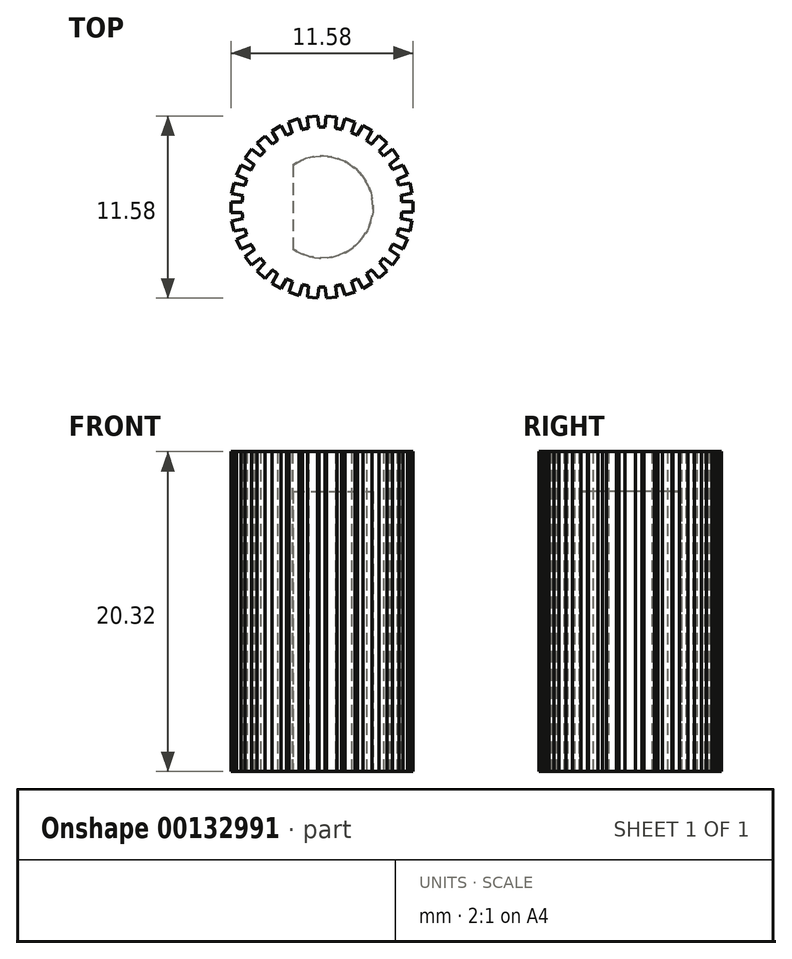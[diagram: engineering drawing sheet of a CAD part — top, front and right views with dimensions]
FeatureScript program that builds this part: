
annotation { "Feature Type Name" : "Feature", "Feature Type Description" : "" }
export const myFeature = defineFeature(function(context is Context, id is Id, definition is map)
    precondition{}
    {
        {
            var Q0;
            Q0=qCreatedBy(makeId("Top.planeOp"),FACE);
            var sketch = newSketch(context, id + "F0", { "sketchPlane" : qUnion([Q0])});
            skArc(sketch, "E0", {"start": v(-1.84, -2.66) * mm, "mid": v(3.24, 0) * mm, "end": v(-1.84, 2.66) * mm});
            skLineSegment(sketch, "E1", {"start": v(-1.84, -0.03) * mm, "end": v(-1.84, 2.66) * mm});
            skLineSegment(sketch, "E2", {"start": v(-1.84, -0.03) * mm, "end": v(-1.84, -2.66) * mm});
            skPoint(sketch, "E3.start.orphan", {"position": v(3.24, 0) * mm});
            skArc(sketch, "E4", {"start": v(-5.07, -0.34) * mm, "mid": v(-5.05, -0.54) * mm, "end": v(-5.03, -0.73) * mm});
            skLineSegment(sketch, "E5", {"start": v(-5.07, 0.33) * mm, "end": v(-5.79, 0.33) * mm});
            skLineSegment(sketch, "E6", {"start": v(-5.79, 0.33) * mm, "end": v(-5.79, 0) * mm});
            skLineSegment(sketch, "E7", {"start": v(-5.79, 0) * mm, "end": v(-5.79, -0.34) * mm});
            skLineSegment(sketch, "E8", {"start": v(-5.79, -0.34) * mm, "end": v(-5.07, -0.34) * mm});
            skLineSegment(sketch, "E9.1.0", {"start": v(-5.03, -0.73) * mm, "end": v(-5.73, -0.88) * mm});
            skLineSegment(sketch, "E9.1.1", {"start": v(-5.66, -1.2) * mm, "end": v(-5.59, -1.53) * mm});
            skLineSegment(sketch, "E9.1.2", {"start": v(-5.73, -0.88) * mm, "end": v(-5.66, -1.2) * mm});
            skLineSegment(sketch, "E9.1.3", {"start": v(-5.59, -1.53) * mm, "end": v(-4.89, -1.38) * mm});
            skLineSegment(sketch, "E9.2.0", {"start": v(-4.77, -1.76) * mm, "end": v(-5.42, -2.05) * mm});
            skLineSegment(sketch, "E9.2.1", {"start": v(-5.29, -2.35) * mm, "end": v(-5.15, -2.66) * mm});
            skLineSegment(sketch, "E9.2.2", {"start": v(-5.42, -2.05) * mm, "end": v(-5.29, -2.35) * mm});
            skLineSegment(sketch, "E9.2.3", {"start": v(-5.15, -2.66) * mm, "end": v(-4.5, -2.37) * mm});
            skLineSegment(sketch, "E9.3.0", {"start": v(-4.3, -2.71) * mm, "end": v(-4.87, -3.13) * mm});
            skLineSegment(sketch, "E9.3.1", {"start": v(-4.68, -3.4) * mm, "end": v(-4.48, -3.67) * mm});
            skLineSegment(sketch, "E9.3.2", {"start": v(-4.87, -3.13) * mm, "end": v(-4.68, -3.4) * mm});
            skLineSegment(sketch, "E9.3.3", {"start": v(-4.48, -3.67) * mm, "end": v(-3.9, -3.25) * mm});
            skLineSegment(sketch, "E9.4.0", {"start": v(-3.64, -3.55) * mm, "end": v(-4.12, -4.08) * mm});
            skLineSegment(sketch, "E9.4.1", {"start": v(-3.87, -4.3) * mm, "end": v(-3.62, -4.53) * mm});
            skLineSegment(sketch, "E9.4.2", {"start": v(-4.12, -4.08) * mm, "end": v(-3.87, -4.3) * mm});
            skLineSegment(sketch, "E9.4.3", {"start": v(-3.62, -4.53) * mm, "end": v(-3.14, -4) * mm});
            skLineSegment(sketch, "E9.5.0", {"start": v(-2.82, -4.23) * mm, "end": v(-3.18, -4.85) * mm});
            skLineSegment(sketch, "E9.5.1", {"start": v(-2.9, -5.01) * mm, "end": v(-2.6, -5.18) * mm});
            skLineSegment(sketch, "E9.5.2", {"start": v(-3.18, -4.85) * mm, "end": v(-2.9, -5.01) * mm});
            skLineSegment(sketch, "E9.5.3", {"start": v(-2.6, -5.18) * mm, "end": v(-2.24, -4.56) * mm});
            skLineSegment(sketch, "E9.6.0", {"start": v(-1.88, -4.72) * mm, "end": v(-2.1, -5.4) * mm});
            skLineSegment(sketch, "E9.6.1", {"start": v(-1.79, -5.5) * mm, "end": v(-1.47, -5.6) * mm});
            skLineSegment(sketch, "E9.6.2", {"start": v(-2.1, -5.4) * mm, "end": v(-1.79, -5.5) * mm});
            skLineSegment(sketch, "E9.6.3", {"start": v(-1.47, -5.6) * mm, "end": v(-1.24, -4.93) * mm});
            skLineSegment(sketch, "E9.7.0", {"start": v(-0.86, -5) * mm, "end": v(-0.93, -5.72) * mm});
            skLineSegment(sketch, "E9.7.1", {"start": v(-0.6, -5.75) * mm, "end": v(-0.27, -5.79) * mm});
            skLineSegment(sketch, "E9.7.2", {"start": v(-0.93, -5.72) * mm, "end": v(-0.6, -5.75) * mm});
            skLineSegment(sketch, "E9.7.3", {"start": v(-0.27, -5.79) * mm, "end": v(-0.2, -5.08) * mm});
            skLineSegment(sketch, "E9.8.0", {"start": v(0.2, -5.08) * mm, "end": v(0.28, -5.79) * mm});
            skLineSegment(sketch, "E9.8.1", {"start": v(0.6, -5.75) * mm, "end": v(0.94, -5.72) * mm});
            skLineSegment(sketch, "E9.8.2", {"start": v(0.28, -5.79) * mm, "end": v(0.6, -5.75) * mm});
            skLineSegment(sketch, "E9.8.3", {"start": v(0.94, -5.72) * mm, "end": v(0.87, -5) * mm});
            skLineSegment(sketch, "E9.9.0", {"start": v(1.25, -4.92) * mm, "end": v(1.47, -5.6) * mm});
            skLineSegment(sketch, "E9.9.1", {"start": v(1.79, -5.5) * mm, "end": v(2.1, -5.4) * mm});
            skLineSegment(sketch, "E9.9.2", {"start": v(1.47, -5.6) * mm, "end": v(1.79, -5.5) * mm});
            skLineSegment(sketch, "E9.9.3", {"start": v(2.1, -5.4) * mm, "end": v(1.89, -4.72) * mm});
            skLineSegment(sketch, "E9.10.0", {"start": v(2.25, -4.56) * mm, "end": v(2.6, -5.18) * mm});
            skLineSegment(sketch, "E9.10.1", {"start": v(2.9, -5.01) * mm, "end": v(3.19, -4.84) * mm});
            skLineSegment(sketch, "E9.10.2", {"start": v(2.6, -5.18) * mm, "end": v(2.9, -5.01) * mm});
            skLineSegment(sketch, "E9.10.3", {"start": v(3.19, -4.84) * mm, "end": v(2.83, -4.22) * mm});
            skLineSegment(sketch, "E9.11.0", {"start": v(3.15, -3.99) * mm, "end": v(3.63, -4.52) * mm});
            skLineSegment(sketch, "E9.11.1", {"start": v(3.87, -4.3) * mm, "end": v(4.12, -4.07) * mm});
            skLineSegment(sketch, "E9.11.2", {"start": v(3.63, -4.52) * mm, "end": v(3.87, -4.3) * mm});
            skLineSegment(sketch, "E9.11.3", {"start": v(4.12, -4.07) * mm, "end": v(3.64, -3.54) * mm});
            skLineSegment(sketch, "E9.12.0", {"start": v(3.9, -3.25) * mm, "end": v(4.49, -3.67) * mm});
            skLineSegment(sketch, "E9.12.1", {"start": v(4.68, -3.4) * mm, "end": v(4.88, -3.13) * mm});
            skLineSegment(sketch, "E9.12.2", {"start": v(4.49, -3.67) * mm, "end": v(4.68, -3.4) * mm});
            skLineSegment(sketch, "E9.12.3", {"start": v(4.88, -3.13) * mm, "end": v(4.3, -2.7) * mm});
            skLineSegment(sketch, "E9.13.0", {"start": v(4.5, -2.36) * mm, "end": v(5.15, -2.65) * mm});
            skLineSegment(sketch, "E9.13.1", {"start": v(5.29, -2.35) * mm, "end": v(5.42, -2.04) * mm});
            skLineSegment(sketch, "E9.13.2", {"start": v(5.15, -2.65) * mm, "end": v(5.29, -2.35) * mm});
            skLineSegment(sketch, "E9.13.3", {"start": v(5.42, -2.04) * mm, "end": v(4.77, -1.75) * mm});
            skLineSegment(sketch, "E9.14.0", {"start": v(4.89, -1.38) * mm, "end": v(5.6, -1.53) * mm});
            skLineSegment(sketch, "E9.14.1", {"start": v(5.66, -1.2) * mm, "end": v(5.73, -0.87) * mm});
            skLineSegment(sketch, "E9.14.2", {"start": v(5.6, -1.53) * mm, "end": v(5.66, -1.2) * mm});
            skLineSegment(sketch, "E9.14.3", {"start": v(5.73, -0.87) * mm, "end": v(5.03, -0.72) * mm});
            skLineSegment(sketch, "E9.15.0", {"start": v(5.07, -0.33) * mm, "end": v(5.79, -0.33) * mm});
            skLineSegment(sketch, "E9.15.1", {"start": v(5.79, 0) * mm, "end": v(5.79, 0.34) * mm});
            skLineSegment(sketch, "E9.15.2", {"start": v(5.79, -0.33) * mm, "end": v(5.79, 0) * mm});
            skLineSegment(sketch, "E9.15.3", {"start": v(5.79, 0.34) * mm, "end": v(5.07, 0.34) * mm});
            skLineSegment(sketch, "E9.16.0", {"start": v(5.03, 0.73) * mm, "end": v(5.73, 0.88) * mm});
            skLineSegment(sketch, "E9.16.1", {"start": v(5.66, 1.2) * mm, "end": v(5.59, 1.53) * mm});
            skLineSegment(sketch, "E9.16.2", {"start": v(5.73, 0.88) * mm, "end": v(5.66, 1.2) * mm});
            skLineSegment(sketch, "E9.16.3", {"start": v(5.59, 1.53) * mm, "end": v(4.89, 1.38) * mm});
            skLineSegment(sketch, "E9.17.0", {"start": v(4.77, 1.76) * mm, "end": v(5.42, 2.05) * mm});
            skLineSegment(sketch, "E9.17.1", {"start": v(5.29, 2.35) * mm, "end": v(5.15, 2.66) * mm});
            skLineSegment(sketch, "E9.17.2", {"start": v(5.42, 2.05) * mm, "end": v(5.29, 2.35) * mm});
            skLineSegment(sketch, "E9.17.3", {"start": v(5.15, 2.66) * mm, "end": v(4.5, 2.37) * mm});
            skLineSegment(sketch, "E9.18.0", {"start": v(4.3, 2.71) * mm, "end": v(4.87, 3.13) * mm});
            skLineSegment(sketch, "E9.18.1", {"start": v(4.68, 3.4) * mm, "end": v(4.48, 3.67) * mm});
            skLineSegment(sketch, "E9.18.2", {"start": v(4.87, 3.13) * mm, "end": v(4.68, 3.4) * mm});
            skLineSegment(sketch, "E9.18.3", {"start": v(4.48, 3.67) * mm, "end": v(3.9, 3.25) * mm});
            skLineSegment(sketch, "E9.19.0", {"start": v(3.64, 3.55) * mm, "end": v(4.12, 4.08) * mm});
            skLineSegment(sketch, "E9.19.1", {"start": v(3.87, 4.3) * mm, "end": v(3.62, 4.53) * mm});
            skLineSegment(sketch, "E9.19.2", {"start": v(4.12, 4.08) * mm, "end": v(3.87, 4.3) * mm});
            skLineSegment(sketch, "E9.19.3", {"start": v(3.62, 4.53) * mm, "end": v(3.14, 4) * mm});
            skLineSegment(sketch, "E9.20.0", {"start": v(2.82, 4.23) * mm, "end": v(3.18, 4.85) * mm});
            skLineSegment(sketch, "E9.20.1", {"start": v(2.9, 5.01) * mm, "end": v(2.6, 5.18) * mm});
            skLineSegment(sketch, "E9.20.2", {"start": v(3.18, 4.85) * mm, "end": v(2.9, 5.01) * mm});
            skLineSegment(sketch, "E9.20.3", {"start": v(2.6, 5.18) * mm, "end": v(2.24, 4.56) * mm});
            skLineSegment(sketch, "E9.21.0", {"start": v(1.88, 4.72) * mm, "end": v(2.1, 5.4) * mm});
            skLineSegment(sketch, "E9.21.1", {"start": v(1.79, 5.5) * mm, "end": v(1.47, 5.6) * mm});
            skLineSegment(sketch, "E9.21.2", {"start": v(2.1, 5.4) * mm, "end": v(1.79, 5.5) * mm});
            skLineSegment(sketch, "E9.21.3", {"start": v(1.47, 5.6) * mm, "end": v(1.24, 4.93) * mm});
            skLineSegment(sketch, "E9.22.0", {"start": v(0.86, 5) * mm, "end": v(0.93, 5.72) * mm});
            skLineSegment(sketch, "E9.22.1", {"start": v(0.6, 5.75) * mm, "end": v(0.27, 5.79) * mm});
            skLineSegment(sketch, "E9.22.2", {"start": v(0.93, 5.72) * mm, "end": v(0.6, 5.75) * mm});
            skLineSegment(sketch, "E9.22.3", {"start": v(0.27, 5.79) * mm, "end": v(0.2, 5.08) * mm});
            skLineSegment(sketch, "E9.23.0", {"start": v(-0.2, 5.08) * mm, "end": v(-0.28, 5.79) * mm});
            skLineSegment(sketch, "E9.23.1", {"start": v(-0.6, 5.75) * mm, "end": v(-0.94, 5.72) * mm});
            skLineSegment(sketch, "E9.23.2", {"start": v(-0.28, 5.79) * mm, "end": v(-0.6, 5.75) * mm});
            skLineSegment(sketch, "E9.23.3", {"start": v(-0.94, 5.72) * mm, "end": v(-0.87, 5) * mm});
            skLineSegment(sketch, "E9.24.0", {"start": v(-1.25, 4.92) * mm, "end": v(-1.47, 5.6) * mm});
            skLineSegment(sketch, "E9.24.1", {"start": v(-1.79, 5.5) * mm, "end": v(-2.1, 5.4) * mm});
            skLineSegment(sketch, "E9.24.2", {"start": v(-1.47, 5.6) * mm, "end": v(-1.79, 5.5) * mm});
            skLineSegment(sketch, "E9.24.3", {"start": v(-2.1, 5.4) * mm, "end": v(-1.89, 4.72) * mm});
            skLineSegment(sketch, "E9.25.0", {"start": v(-2.25, 4.56) * mm, "end": v(-2.6, 5.18) * mm});
            skLineSegment(sketch, "E9.25.1", {"start": v(-2.9, 5.01) * mm, "end": v(-3.19, 4.84) * mm});
            skLineSegment(sketch, "E9.25.2", {"start": v(-2.6, 5.18) * mm, "end": v(-2.9, 5.01) * mm});
            skLineSegment(sketch, "E9.25.3", {"start": v(-3.19, 4.84) * mm, "end": v(-2.83, 4.22) * mm});
            skLineSegment(sketch, "E9.26.0", {"start": v(-3.15, 3.99) * mm, "end": v(-3.63, 4.52) * mm});
            skLineSegment(sketch, "E9.26.1", {"start": v(-3.87, 4.3) * mm, "end": v(-4.12, 4.07) * mm});
            skLineSegment(sketch, "E9.26.2", {"start": v(-3.63, 4.52) * mm, "end": v(-3.87, 4.3) * mm});
            skLineSegment(sketch, "E9.26.3", {"start": v(-4.12, 4.07) * mm, "end": v(-3.64, 3.54) * mm});
            skLineSegment(sketch, "E9.27.0", {"start": v(-3.9, 3.25) * mm, "end": v(-4.49, 3.67) * mm});
            skLineSegment(sketch, "E9.27.1", {"start": v(-4.68, 3.4) * mm, "end": v(-4.88, 3.13) * mm});
            skLineSegment(sketch, "E9.27.2", {"start": v(-4.49, 3.67) * mm, "end": v(-4.68, 3.4) * mm});
            skLineSegment(sketch, "E9.27.3", {"start": v(-4.88, 3.13) * mm, "end": v(-4.3, 2.7) * mm});
            skLineSegment(sketch, "E9.28.0", {"start": v(-4.5, 2.36) * mm, "end": v(-5.15, 2.65) * mm});
            skLineSegment(sketch, "E9.28.1", {"start": v(-5.29, 2.35) * mm, "end": v(-5.42, 2.04) * mm});
            skLineSegment(sketch, "E9.28.2", {"start": v(-5.15, 2.65) * mm, "end": v(-5.29, 2.35) * mm});
            skLineSegment(sketch, "E9.28.3", {"start": v(-5.42, 2.04) * mm, "end": v(-4.77, 1.75) * mm});
            skLineSegment(sketch, "E9.29.0", {"start": v(-4.89, 1.38) * mm, "end": v(-5.6, 1.53) * mm});
            skLineSegment(sketch, "E9.29.1", {"start": v(-5.66, 1.2) * mm, "end": v(-5.73, 0.87) * mm});
            skLineSegment(sketch, "E9.29.2", {"start": v(-5.6, 1.53) * mm, "end": v(-5.66, 1.2) * mm});
            skLineSegment(sketch, "E9.29.3", {"start": v(-5.73, 0.87) * mm, "end": v(-5.03, 0.72) * mm});
            skArc(sketch, "E10.trimOffspring", {"start": v(-5.03, 0.72) * mm, "mid": v(-5.05, 0.53) * mm, "end": v(-5.07, 0.33) * mm});
            skArc(sketch, "E11.trimOffspring", {"start": v(-4.77, 1.75) * mm, "mid": v(-4.83, 1.57) * mm, "end": v(-4.89, 1.38) * mm});
            skArc(sketch, "E12.trimOffspring", {"start": v(-4.3, 2.7) * mm, "mid": v(-4.4, 2.54) * mm, "end": v(-4.5, 2.36) * mm});
            skArc(sketch, "E13.trimOffspring", {"start": v(-3.64, 3.54) * mm, "mid": v(-3.78, 3.4) * mm, "end": v(-3.9, 3.25) * mm});
            skArc(sketch, "E14.trimOffspring", {"start": v(-2.83, 4.22) * mm, "mid": v(-2.99, 4.1) * mm, "end": v(-3.15, 3.99) * mm});
            skArc(sketch, "E15.trimOffspring", {"start": v(-1.89, 4.72) * mm, "mid": v(-2.07, 4.64) * mm, "end": v(-2.25, 4.56) * mm});
            skArc(sketch, "E16.trimOffspring", {"start": v(-0.87, 5) * mm, "mid": v(-1.06, 4.97) * mm, "end": v(-1.25, 4.92) * mm});
            skArc(sketch, "E17.trimOffspring", {"start": v(0.2, 5.08) * mm, "mid": v(0, 5.08) * mm, "end": v(-0.2, 5.08) * mm});
            skArc(sketch, "E18.trimOffspring", {"start": v(1.24, 4.93) * mm, "mid": v(1.05, 4.97) * mm, "end": v(0.86, 5) * mm});
            skArc(sketch, "E19.trimOffspring", {"start": v(2.24, 4.56) * mm, "mid": v(2.06, 4.64) * mm, "end": v(1.88, 4.72) * mm});
            skArc(sketch, "E20.trimOffspring", {"start": v(3.14, 4) * mm, "mid": v(2.98, 4.11) * mm, "end": v(2.82, 4.23) * mm});
            skArc(sketch, "E21.trimOffspring", {"start": v(3.9, 3.25) * mm, "mid": v(3.77, 3.4) * mm, "end": v(3.64, 3.55) * mm});
            skArc(sketch, "E22.trimOffspring", {"start": v(4.5, 2.37) * mm, "mid": v(4.4, 2.54) * mm, "end": v(4.3, 2.71) * mm});
            skArc(sketch, "E23.trimOffspring", {"start": v(4.89, 1.38) * mm, "mid": v(4.83, 1.57) * mm, "end": v(4.77, 1.76) * mm});
            skArc(sketch, "E24.trimOffspring", {"start": v(5.07, 0.34) * mm, "mid": v(5.05, 0.54) * mm, "end": v(5.03, 0.73) * mm});
            skArc(sketch, "E25.trimOffspring", {"start": v(5.03, -0.72) * mm, "mid": v(5.05, -0.53) * mm, "end": v(5.07, -0.33) * mm});
            skArc(sketch, "E26.trimOffspring", {"start": v(4.77, -1.75) * mm, "mid": v(4.83, -1.57) * mm, "end": v(4.89, -1.38) * mm});
            skArc(sketch, "E27.trimOffspring", {"start": v(4.3, -2.7) * mm, "mid": v(4.4, -2.54) * mm, "end": v(4.5, -2.36) * mm});
            skArc(sketch, "E28.trimOffspring", {"start": v(3.64, -3.54) * mm, "mid": v(3.78, -3.4) * mm, "end": v(3.9, -3.25) * mm});
            skArc(sketch, "E29.trimOffspring", {"start": v(2.83, -4.22) * mm, "mid": v(2.99, -4.1) * mm, "end": v(3.15, -3.99) * mm});
            skArc(sketch, "E30.trimOffspring", {"start": v(1.89, -4.72) * mm, "mid": v(2.07, -4.64) * mm, "end": v(2.25, -4.56) * mm});
            skArc(sketch, "E31.trimOffspring", {"start": v(0.87, -5) * mm, "mid": v(1.06, -4.97) * mm, "end": v(1.25, -4.92) * mm});
            skArc(sketch, "E32.trimOffspring", {"start": v(-0.2, -5.08) * mm, "mid": v(0, -5.08) * mm, "end": v(0.2, -5.08) * mm});
            skArc(sketch, "E33.trimOffspring", {"start": v(-1.24, -4.93) * mm, "mid": v(-1.05, -4.97) * mm, "end": v(-0.86, -5) * mm});
            skArc(sketch, "E34.trimOffspring", {"start": v(-2.24, -4.56) * mm, "mid": v(-2.06, -4.64) * mm, "end": v(-1.88, -4.72) * mm});
            skArc(sketch, "E35.trimOffspring", {"start": v(-3.14, -4) * mm, "mid": v(-2.98, -4.11) * mm, "end": v(-2.82, -4.23) * mm});
            skArc(sketch, "E36.trimOffspring", {"start": v(-3.9, -3.25) * mm, "mid": v(-3.77, -3.4) * mm, "end": v(-3.64, -3.55) * mm});
            skArc(sketch, "E37.trimOffspring", {"start": v(-4.5, -2.37) * mm, "mid": v(-4.4, -2.54) * mm, "end": v(-4.3, -2.71) * mm});
            skArc(sketch, "E38.trimOffspring", {"start": v(-4.89, -1.38) * mm, "mid": v(-4.83, -1.57) * mm, "end": v(-4.77, -1.76) * mm});
            skSolve(sketch);
        }
        {
            var Q0;
            Q0=makeQuery(id+"F0.imprint","IMPRINT",FACE,{"disambiguationData":[TD([[makeQuery(id+"F0.imprint","IMPRINT",EDGE,{"derivedFrom":sQuery(id+"F0.wireOp",EDGE,"E0")}),-1.0]])]});
            extrude(context, id + "F1", {"entities" : qUnion([Q0]), "depth" : 15.24 * mm});
        }
        {
            var Q0;
            Q0=makeQuery(id+"F1.opExtrude","CAP_FACE",FACE,{"disambiguationData":[OSD([sQuery(id+"F0.wireOp",EDGE,"E0"),sQuery(id+"F0.wireOp",EDGE,"E1"),sQuery(id+"F0.wireOp",EDGE,"E2"),sQuery(id+"F0.wireOp",EDGE,"E4"),sQuery(id+"F0.wireOp",EDGE,"E5"),sQuery(id+"F0.wireOp",EDGE,"E6"),sQuery(id+"F0.wireOp",EDGE,"E7"),sQuery(id+"F0.wireOp",EDGE,"E8"),sQuery(id+"F0.wireOp",EDGE,"E9.1.0"),sQuery(id+"F0.wireOp",EDGE,"E9.1.1"),sQuery(id+"F0.wireOp",EDGE,"E9.1.2"),sQuery(id+"F0.wireOp",EDGE,"E9.1.3"),sQuery(id+"F0.wireOp",EDGE,"E9.2.0"),sQuery(id+"F0.wireOp",EDGE,"E9.2.1"),sQuery(id+"F0.wireOp",EDGE,"E9.2.2"),sQuery(id+"F0.wireOp",EDGE,"E9.2.3"),sQuery(id+"F0.wireOp",EDGE,"E9.3.0"),sQuery(id+"F0.wireOp",EDGE,"E9.3.1"),sQuery(id+"F0.wireOp",EDGE,"E9.3.2"),sQuery(id+"F0.wireOp",EDGE,"E9.3.3"),sQuery(id+"F0.wireOp",EDGE,"E9.4.0"),sQuery(id+"F0.wireOp",EDGE,"E9.4.1"),sQuery(id+"F0.wireOp",EDGE,"E9.4.2"),sQuery(id+"F0.wireOp",EDGE,"E9.4.3"),sQuery(id+"F0.wireOp",EDGE,"E9.5.0"),sQuery(id+"F0.wireOp",EDGE,"E9.5.1"),sQuery(id+"F0.wireOp",EDGE,"E9.5.2"),sQuery(id+"F0.wireOp",EDGE,"E9.5.3"),sQuery(id+"F0.wireOp",EDGE,"E9.6.0"),sQuery(id+"F0.wireOp",EDGE,"E9.6.1"),sQuery(id+"F0.wireOp",EDGE,"E9.6.2"),sQuery(id+"F0.wireOp",EDGE,"E9.6.3"),sQuery(id+"F0.wireOp",EDGE,"E9.7.0"),sQuery(id+"F0.wireOp",EDGE,"E9.7.1"),sQuery(id+"F0.wireOp",EDGE,"E9.7.2"),sQuery(id+"F0.wireOp",EDGE,"E9.7.3"),sQuery(id+"F0.wireOp",EDGE,"E9.8.0"),sQuery(id+"F0.wireOp",EDGE,"E9.8.1"),sQuery(id+"F0.wireOp",EDGE,"E9.8.2"),sQuery(id+"F0.wireOp",EDGE,"E9.8.3"),sQuery(id+"F0.wireOp",EDGE,"E9.9.0"),sQuery(id+"F0.wireOp",EDGE,"E9.9.1"),sQuery(id+"F0.wireOp",EDGE,"E9.9.2"),sQuery(id+"F0.wireOp",EDGE,"E9.9.3"),sQuery(id+"F0.wireOp",EDGE,"E9.10.0"),sQuery(id+"F0.wireOp",EDGE,"E9.10.1"),sQuery(id+"F0.wireOp",EDGE,"E9.10.2"),sQuery(id+"F0.wireOp",EDGE,"E9.10.3"),sQuery(id+"F0.wireOp",EDGE,"E9.11.0"),sQuery(id+"F0.wireOp",EDGE,"E9.11.1"),sQuery(id+"F0.wireOp",EDGE,"E9.11.2"),sQuery(id+"F0.wireOp",EDGE,"E9.11.3"),sQuery(id+"F0.wireOp",EDGE,"E9.12.0"),sQuery(id+"F0.wireOp",EDGE,"E9.12.1"),sQuery(id+"F0.wireOp",EDGE,"E9.12.2"),sQuery(id+"F0.wireOp",EDGE,"E9.12.3"),sQuery(id+"F0.wireOp",EDGE,"E9.13.0"),sQuery(id+"F0.wireOp",EDGE,"E9.13.1"),sQuery(id+"F0.wireOp",EDGE,"E9.13.2"),sQuery(id+"F0.wireOp",EDGE,"E9.13.3"),sQuery(id+"F0.wireOp",EDGE,"E9.14.0"),sQuery(id+"F0.wireOp",EDGE,"E9.14.1"),sQuery(id+"F0.wireOp",EDGE,"E9.14.2"),sQuery(id+"F0.wireOp",EDGE,"E9.14.3"),sQuery(id+"F0.wireOp",EDGE,"E9.15.0"),sQuery(id+"F0.wireOp",EDGE,"E9.15.1"),sQuery(id+"F0.wireOp",EDGE,"E9.15.2"),sQuery(id+"F0.wireOp",EDGE,"E9.15.3"),sQuery(id+"F0.wireOp",EDGE,"E9.16.0"),sQuery(id+"F0.wireOp",EDGE,"E9.16.1"),sQuery(id+"F0.wireOp",EDGE,"E9.16.2"),sQuery(id+"F0.wireOp",EDGE,"E9.16.3"),sQuery(id+"F0.wireOp",EDGE,"E9.17.0"),sQuery(id+"F0.wireOp",EDGE,"E9.17.1"),sQuery(id+"F0.wireOp",EDGE,"E9.17.2"),sQuery(id+"F0.wireOp",EDGE,"E9.17.3"),sQuery(id+"F0.wireOp",EDGE,"E9.18.0"),sQuery(id+"F0.wireOp",EDGE,"E9.18.1"),sQuery(id+"F0.wireOp",EDGE,"E9.18.2"),sQuery(id+"F0.wireOp",EDGE,"E9.18.3"),sQuery(id+"F0.wireOp",EDGE,"E9.19.0"),sQuery(id+"F0.wireOp",EDGE,"E9.19.1"),sQuery(id+"F0.wireOp",EDGE,"E9.19.2"),sQuery(id+"F0.wireOp",EDGE,"E9.19.3"),sQuery(id+"F0.wireOp",EDGE,"E9.20.0"),sQuery(id+"F0.wireOp",EDGE,"E9.20.1"),sQuery(id+"F0.wireOp",EDGE,"E9.20.2"),sQuery(id+"F0.wireOp",EDGE,"E9.20.3"),sQuery(id+"F0.wireOp",EDGE,"E9.21.0"),sQuery(id+"F0.wireOp",EDGE,"E9.21.1"),sQuery(id+"F0.wireOp",EDGE,"E9.21.2"),sQuery(id+"F0.wireOp",EDGE,"E9.21.3"),sQuery(id+"F0.wireOp",EDGE,"E9.22.0"),sQuery(id+"F0.wireOp",EDGE,"E9.22.1"),sQuery(id+"F0.wireOp",EDGE,"E9.22.2"),sQuery(id+"F0.wireOp",EDGE,"E9.22.3"),sQuery(id+"F0.wireOp",EDGE,"E9.23.0"),sQuery(id+"F0.wireOp",EDGE,"E9.23.1"),sQuery(id+"F0.wireOp",EDGE,"E9.23.2"),sQuery(id+"F0.wireOp",EDGE,"E9.23.3"),sQuery(id+"F0.wireOp",EDGE,"E9.24.0"),sQuery(id+"F0.wireOp",EDGE,"E9.24.1"),sQuery(id+"F0.wireOp",EDGE,"E9.24.2"),sQuery(id+"F0.wireOp",EDGE,"E9.24.3"),sQuery(id+"F0.wireOp",EDGE,"E9.25.0"),sQuery(id+"F0.wireOp",EDGE,"E9.25.1"),sQuery(id+"F0.wireOp",EDGE,"E9.25.2"),sQuery(id+"F0.wireOp",EDGE,"E9.25.3"),sQuery(id+"F0.wireOp",EDGE,"E9.26.0"),sQuery(id+"F0.wireOp",EDGE,"E9.26.1"),sQuery(id+"F0.wireOp",EDGE,"E9.26.2"),sQuery(id+"F0.wireOp",EDGE,"E9.26.3"),sQuery(id+"F0.wireOp",EDGE,"E9.27.0"),sQuery(id+"F0.wireOp",EDGE,"E9.27.1"),sQuery(id+"F0.wireOp",EDGE,"E9.27.2"),sQuery(id+"F0.wireOp",EDGE,"E9.27.3"),sQuery(id+"F0.wireOp",EDGE,"E9.28.0"),sQuery(id+"F0.wireOp",EDGE,"E9.28.1"),sQuery(id+"F0.wireOp",EDGE,"E9.28.2"),sQuery(id+"F0.wireOp",EDGE,"E9.28.3"),sQuery(id+"F0.wireOp",EDGE,"E9.29.0"),sQuery(id+"F0.wireOp",EDGE,"E9.29.1"),sQuery(id+"F0.wireOp",EDGE,"E9.29.2"),sQuery(id+"F0.wireOp",EDGE,"E9.29.3"),sQuery(id+"F0.wireOp",EDGE,"E10.trimOffspring"),sQuery(id+"F0.wireOp",EDGE,"E11.trimOffspring"),sQuery(id+"F0.wireOp",EDGE,"E12.trimOffspring"),sQuery(id+"F0.wireOp",EDGE,"E13.trimOffspring"),sQuery(id+"F0.wireOp",EDGE,"E14.trimOffspring"),sQuery(id+"F0.wireOp",EDGE,"E15.trimOffspring"),sQuery(id+"F0.wireOp",EDGE,"E16.trimOffspring"),sQuery(id+"F0.wireOp",EDGE,"E17.trimOffspring"),sQuery(id+"F0.wireOp",EDGE,"E18.trimOffspring"),sQuery(id+"F0.wireOp",EDGE,"E19.trimOffspring"),sQuery(id+"F0.wireOp",EDGE,"E20.trimOffspring"),sQuery(id+"F0.wireOp",EDGE,"E21.trimOffspring"),sQuery(id+"F0.wireOp",EDGE,"E22.trimOffspring"),sQuery(id+"F0.wireOp",EDGE,"E23.trimOffspring"),sQuery(id+"F0.wireOp",EDGE,"E24.trimOffspring"),sQuery(id+"F0.wireOp",EDGE,"E25.trimOffspring"),sQuery(id+"F0.wireOp",EDGE,"E26.trimOffspring"),sQuery(id+"F0.wireOp",EDGE,"E27.trimOffspring"),sQuery(id+"F0.wireOp",EDGE,"E28.trimOffspring"),sQuery(id+"F0.wireOp",EDGE,"E29.trimOffspring"),sQuery(id+"F0.wireOp",EDGE,"E30.trimOffspring"),sQuery(id+"F0.wireOp",EDGE,"E31.trimOffspring"),sQuery(id+"F0.wireOp",EDGE,"E32.trimOffspring"),sQuery(id+"F0.wireOp",EDGE,"E33.trimOffspring"),sQuery(id+"F0.wireOp",EDGE,"E34.trimOffspring"),sQuery(id+"F0.wireOp",EDGE,"E35.trimOffspring"),sQuery(id+"F0.wireOp",EDGE,"E36.trimOffspring"),sQuery(id+"F0.wireOp",EDGE,"E37.trimOffspring"),sQuery(id+"F0.wireOp",EDGE,"E38.trimOffspring")])],"isStart":false});
            var sketch = newSketch(context, id + "F2", { "sketchPlane" : qUnion([Q0])});
            skCircle(sketch, "E39", {"center": v(0, 0) * mm, "radius": 3.24 * mm});
            skSolve(sketch);
        }
        {
            var Q0;
            Q0 = qSketchRegion(id + "F2", true);
            extrude(context, id + "F3", {"entities" : qUnion([Q0]), "operationType" : NewBodyOperationType.ADD, "oppositeDirection" : true, "depth" : 2.54 * mm});
        }
        {
            var Q0;
            Q0=makeQuery(id+"F1.opExtrude","CAP_FACE",FACE,{"disambiguationData":[OSD([sQuery(id+"F0.wireOp",EDGE,"E0"),sQuery(id+"F0.wireOp",EDGE,"E1"),sQuery(id+"F0.wireOp",EDGE,"E2"),sQuery(id+"F0.wireOp",EDGE,"E4"),sQuery(id+"F0.wireOp",EDGE,"E5"),sQuery(id+"F0.wireOp",EDGE,"E6"),sQuery(id+"F0.wireOp",EDGE,"E7"),sQuery(id+"F0.wireOp",EDGE,"E8"),sQuery(id+"F0.wireOp",EDGE,"E9.1.0"),sQuery(id+"F0.wireOp",EDGE,"E9.1.1"),sQuery(id+"F0.wireOp",EDGE,"E9.1.2"),sQuery(id+"F0.wireOp",EDGE,"E9.1.3"),sQuery(id+"F0.wireOp",EDGE,"E9.2.0"),sQuery(id+"F0.wireOp",EDGE,"E9.2.1"),sQuery(id+"F0.wireOp",EDGE,"E9.2.2"),sQuery(id+"F0.wireOp",EDGE,"E9.2.3"),sQuery(id+"F0.wireOp",EDGE,"E9.3.0"),sQuery(id+"F0.wireOp",EDGE,"E9.3.1"),sQuery(id+"F0.wireOp",EDGE,"E9.3.2"),sQuery(id+"F0.wireOp",EDGE,"E9.3.3"),sQuery(id+"F0.wireOp",EDGE,"E9.4.0"),sQuery(id+"F0.wireOp",EDGE,"E9.4.1"),sQuery(id+"F0.wireOp",EDGE,"E9.4.2"),sQuery(id+"F0.wireOp",EDGE,"E9.4.3"),sQuery(id+"F0.wireOp",EDGE,"E9.5.0"),sQuery(id+"F0.wireOp",EDGE,"E9.5.1"),sQuery(id+"F0.wireOp",EDGE,"E9.5.2"),sQuery(id+"F0.wireOp",EDGE,"E9.5.3"),sQuery(id+"F0.wireOp",EDGE,"E9.6.0"),sQuery(id+"F0.wireOp",EDGE,"E9.6.1"),sQuery(id+"F0.wireOp",EDGE,"E9.6.2"),sQuery(id+"F0.wireOp",EDGE,"E9.6.3"),sQuery(id+"F0.wireOp",EDGE,"E9.7.0"),sQuery(id+"F0.wireOp",EDGE,"E9.7.1"),sQuery(id+"F0.wireOp",EDGE,"E9.7.2"),sQuery(id+"F0.wireOp",EDGE,"E9.7.3"),sQuery(id+"F0.wireOp",EDGE,"E9.8.0"),sQuery(id+"F0.wireOp",EDGE,"E9.8.1"),sQuery(id+"F0.wireOp",EDGE,"E9.8.2"),sQuery(id+"F0.wireOp",EDGE,"E9.8.3"),sQuery(id+"F0.wireOp",EDGE,"E9.9.0"),sQuery(id+"F0.wireOp",EDGE,"E9.9.1"),sQuery(id+"F0.wireOp",EDGE,"E9.9.2"),sQuery(id+"F0.wireOp",EDGE,"E9.9.3"),sQuery(id+"F0.wireOp",EDGE,"E9.10.0"),sQuery(id+"F0.wireOp",EDGE,"E9.10.1"),sQuery(id+"F0.wireOp",EDGE,"E9.10.2"),sQuery(id+"F0.wireOp",EDGE,"E9.10.3"),sQuery(id+"F0.wireOp",EDGE,"E9.11.0"),sQuery(id+"F0.wireOp",EDGE,"E9.11.1"),sQuery(id+"F0.wireOp",EDGE,"E9.11.2"),sQuery(id+"F0.wireOp",EDGE,"E9.11.3"),sQuery(id+"F0.wireOp",EDGE,"E9.12.0"),sQuery(id+"F0.wireOp",EDGE,"E9.12.1"),sQuery(id+"F0.wireOp",EDGE,"E9.12.2"),sQuery(id+"F0.wireOp",EDGE,"E9.12.3"),sQuery(id+"F0.wireOp",EDGE,"E9.13.0"),sQuery(id+"F0.wireOp",EDGE,"E9.13.1"),sQuery(id+"F0.wireOp",EDGE,"E9.13.2"),sQuery(id+"F0.wireOp",EDGE,"E9.13.3"),sQuery(id+"F0.wireOp",EDGE,"E9.14.0"),sQuery(id+"F0.wireOp",EDGE,"E9.14.1"),sQuery(id+"F0.wireOp",EDGE,"E9.14.2"),sQuery(id+"F0.wireOp",EDGE,"E9.14.3"),sQuery(id+"F0.wireOp",EDGE,"E9.15.0"),sQuery(id+"F0.wireOp",EDGE,"E9.15.1"),sQuery(id+"F0.wireOp",EDGE,"E9.15.2"),sQuery(id+"F0.wireOp",EDGE,"E9.15.3"),sQuery(id+"F0.wireOp",EDGE,"E9.16.0"),sQuery(id+"F0.wireOp",EDGE,"E9.16.1"),sQuery(id+"F0.wireOp",EDGE,"E9.16.2"),sQuery(id+"F0.wireOp",EDGE,"E9.16.3"),sQuery(id+"F0.wireOp",EDGE,"E9.17.0"),sQuery(id+"F0.wireOp",EDGE,"E9.17.1"),sQuery(id+"F0.wireOp",EDGE,"E9.17.2"),sQuery(id+"F0.wireOp",EDGE,"E9.17.3"),sQuery(id+"F0.wireOp",EDGE,"E9.18.0"),sQuery(id+"F0.wireOp",EDGE,"E9.18.1"),sQuery(id+"F0.wireOp",EDGE,"E9.18.2"),sQuery(id+"F0.wireOp",EDGE,"E9.18.3"),sQuery(id+"F0.wireOp",EDGE,"E9.19.0"),sQuery(id+"F0.wireOp",EDGE,"E9.19.1"),sQuery(id+"F0.wireOp",EDGE,"E9.19.2"),sQuery(id+"F0.wireOp",EDGE,"E9.19.3"),sQuery(id+"F0.wireOp",EDGE,"E9.20.0"),sQuery(id+"F0.wireOp",EDGE,"E9.20.1"),sQuery(id+"F0.wireOp",EDGE,"E9.20.2"),sQuery(id+"F0.wireOp",EDGE,"E9.20.3"),sQuery(id+"F0.wireOp",EDGE,"E9.21.0"),sQuery(id+"F0.wireOp",EDGE,"E9.21.1"),sQuery(id+"F0.wireOp",EDGE,"E9.21.2"),sQuery(id+"F0.wireOp",EDGE,"E9.21.3"),sQuery(id+"F0.wireOp",EDGE,"E9.22.0"),sQuery(id+"F0.wireOp",EDGE,"E9.22.1"),sQuery(id+"F0.wireOp",EDGE,"E9.22.2"),sQuery(id+"F0.wireOp",EDGE,"E9.22.3"),sQuery(id+"F0.wireOp",EDGE,"E9.23.0"),sQuery(id+"F0.wireOp",EDGE,"E9.23.1"),sQuery(id+"F0.wireOp",EDGE,"E9.23.2"),sQuery(id+"F0.wireOp",EDGE,"E9.23.3"),sQuery(id+"F0.wireOp",EDGE,"E9.24.0"),sQuery(id+"F0.wireOp",EDGE,"E9.24.1"),sQuery(id+"F0.wireOp",EDGE,"E9.24.2"),sQuery(id+"F0.wireOp",EDGE,"E9.24.3"),sQuery(id+"F0.wireOp",EDGE,"E9.25.0"),sQuery(id+"F0.wireOp",EDGE,"E9.25.1"),sQuery(id+"F0.wireOp",EDGE,"E9.25.2"),sQuery(id+"F0.wireOp",EDGE,"E9.25.3"),sQuery(id+"F0.wireOp",EDGE,"E9.26.0"),sQuery(id+"F0.wireOp",EDGE,"E9.26.1"),sQuery(id+"F0.wireOp",EDGE,"E9.26.2"),sQuery(id+"F0.wireOp",EDGE,"E9.26.3"),sQuery(id+"F0.wireOp",EDGE,"E9.27.0"),sQuery(id+"F0.wireOp",EDGE,"E9.27.1"),sQuery(id+"F0.wireOp",EDGE,"E9.27.2"),sQuery(id+"F0.wireOp",EDGE,"E9.27.3"),sQuery(id+"F0.wireOp",EDGE,"E9.28.0"),sQuery(id+"F0.wireOp",EDGE,"E9.28.1"),sQuery(id+"F0.wireOp",EDGE,"E9.28.2"),sQuery(id+"F0.wireOp",EDGE,"E9.28.3"),sQuery(id+"F0.wireOp",EDGE,"E9.29.0"),sQuery(id+"F0.wireOp",EDGE,"E9.29.1"),sQuery(id+"F0.wireOp",EDGE,"E9.29.2"),sQuery(id+"F0.wireOp",EDGE,"E9.29.3"),sQuery(id+"F0.wireOp",EDGE,"E10.trimOffspring"),sQuery(id+"F0.wireOp",EDGE,"E11.trimOffspring"),sQuery(id+"F0.wireOp",EDGE,"E12.trimOffspring"),sQuery(id+"F0.wireOp",EDGE,"E13.trimOffspring"),sQuery(id+"F0.wireOp",EDGE,"E14.trimOffspring"),sQuery(id+"F0.wireOp",EDGE,"E15.trimOffspring"),sQuery(id+"F0.wireOp",EDGE,"E16.trimOffspring"),sQuery(id+"F0.wireOp",EDGE,"E17.trimOffspring"),sQuery(id+"F0.wireOp",EDGE,"E18.trimOffspring"),sQuery(id+"F0.wireOp",EDGE,"E19.trimOffspring"),sQuery(id+"F0.wireOp",EDGE,"E20.trimOffspring"),sQuery(id+"F0.wireOp",EDGE,"E21.trimOffspring"),sQuery(id+"F0.wireOp",EDGE,"E22.trimOffspring"),sQuery(id+"F0.wireOp",EDGE,"E23.trimOffspring"),sQuery(id+"F0.wireOp",EDGE,"E24.trimOffspring"),sQuery(id+"F0.wireOp",EDGE,"E25.trimOffspring"),sQuery(id+"F0.wireOp",EDGE,"E26.trimOffspring"),sQuery(id+"F0.wireOp",EDGE,"E27.trimOffspring"),sQuery(id+"F0.wireOp",EDGE,"E28.trimOffspring"),sQuery(id+"F0.wireOp",EDGE,"E29.trimOffspring"),sQuery(id+"F0.wireOp",EDGE,"E30.trimOffspring"),sQuery(id+"F0.wireOp",EDGE,"E31.trimOffspring"),sQuery(id+"F0.wireOp",EDGE,"E32.trimOffspring"),sQuery(id+"F0.wireOp",EDGE,"E33.trimOffspring"),sQuery(id+"F0.wireOp",EDGE,"E34.trimOffspring"),sQuery(id+"F0.wireOp",EDGE,"E35.trimOffspring"),sQuery(id+"F0.wireOp",EDGE,"E36.trimOffspring"),sQuery(id+"F0.wireOp",EDGE,"E37.trimOffspring"),sQuery(id+"F0.wireOp",EDGE,"E38.trimOffspring")])],"isStart":true});
            extrude(context, id + "F4", {"entities" : qUnion([Q0]), "operationType" : NewBodyOperationType.ADD, "depth" : 5.08 * mm});
        }
    });
